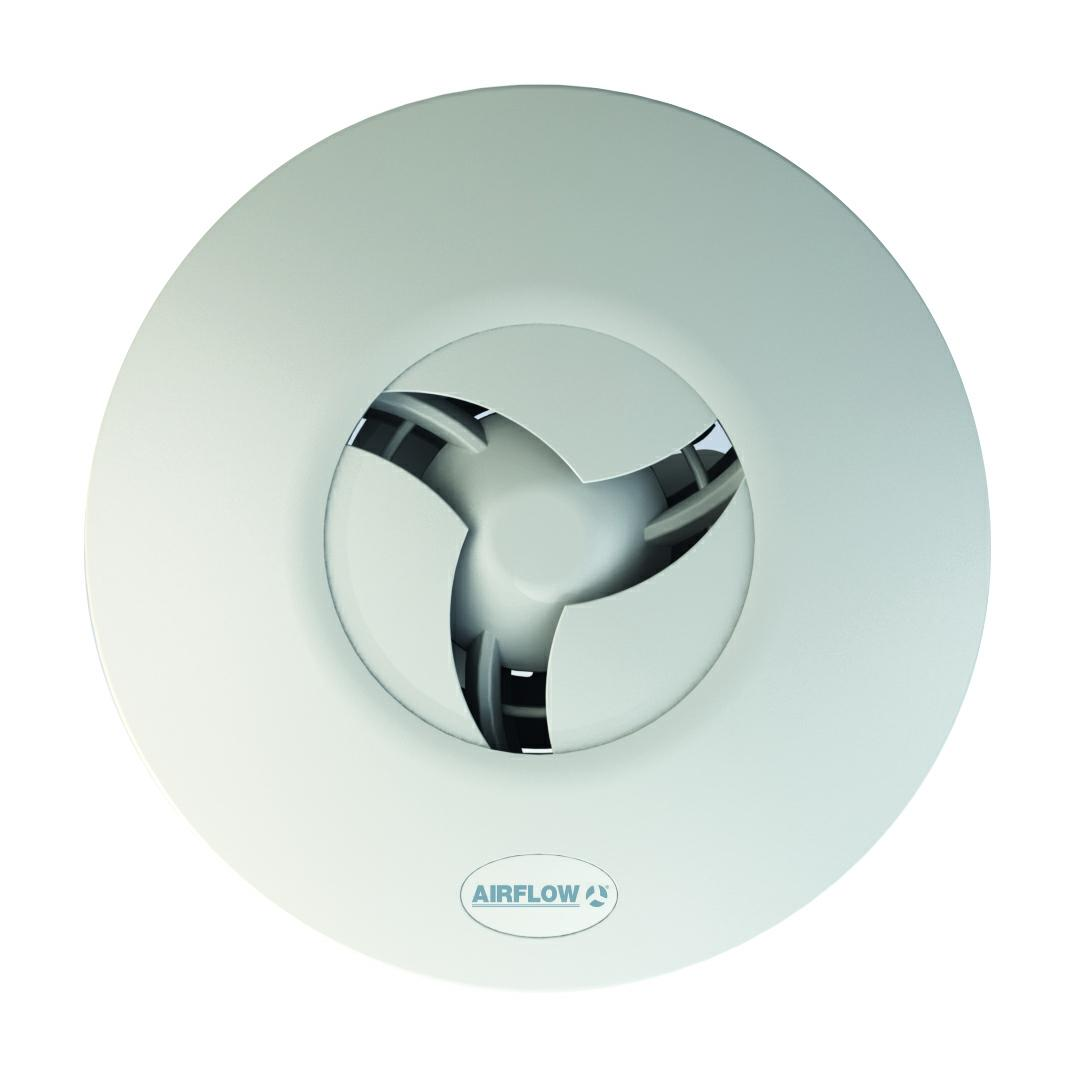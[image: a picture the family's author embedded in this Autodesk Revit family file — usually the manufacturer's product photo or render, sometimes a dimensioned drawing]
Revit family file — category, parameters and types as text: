
# Revit family: CADS_AIRFLOWdev_Fan_iCON15L_Smart
name_source: partatom
category: Mechanical Equipment
revit_build: Autodesk Revit 2016 (Build: 20150220_1215(x64)
units: mm (PartAtom-declared; Revit-internal decimal feet)

## family parameters
Cut with Voids When Loaded = No
Host = Face
Part Type = Normal
Room Calculation Point = No
Round Connector Dimension = Use Diameter
Shared = No

## types (1)
- iCONsmart 15L
    6MonthlyMaintenance = Visually inspect system, clean the fan and ducting if necessary
    A = 194 mm  [stored 0.636483 ft]
    AccessClearanceBottom = 350 mm
    AccessClearanceFront = 350 mm
    AccessClearanceLeft = 350 mm
    AccessClearanceRear = 0 mm  [stored 0 ft]
    AccessClearanceRight = 350 mm
    AccessClearanceTop = 350 mm
    AnthraciteFT = CADS_AIRFLOWdev_Fan_iCON15_Covers : Anthracite
    AssemblyPlace = UKNOWN
    AssetType = Fixed
    BMSLinks = No
    Body = CADS_AirFlow_White
    C = 72 mm  [stored 0.23622 ft]
    CADS_Index = 0
    CEApproval = Yes
    CapacityControlType = Variable Speed Drive
    Category = Pr_65_67_29_05:Axial Flow Fans
    ChromeFT = CADS_AIRFLOWdev_Fan_iCON15_Covers : Chrome
    Color = White
    Controls = Basic on/off functionality controlled by external switch
The following additional, interchangeable modules can be fitted to the iCONsmart15:
Timer (72687224)
Humidity with Timer (72687225)
Motion sensor with timer  (72687226)
Motion sensor humidity timer (72687227)
    D = 100 mm  [stored 0.328084 ft]
    Default Elevation = 1219 mm
    Description = A smart intermittent extract fan with interchangeable modular controls and covers and a Red Dot Design Award winner and Quiet mark certified
    DesignOfDomesticVentilation = This fan should provide the minimum flow rates outlined and installed in line with Approved Document Part F of the Building Regulations.
    Ductwork = 100mm flexible or rigid
    DurationUnit = Year
    E = 46 mm  [stored 0.150919 ft]
    ErPEnergyRating = C
    ErPFiche = https://www.airflow.com
    Exclusions = Hasn't been installed or used in accordance with the instructions
Connected with an unsuitable electrical supply
Has been misused, neglected or damaged
Modified or repaired by someone not authorised by Airflow Developments Ltd
Hasn't been installed according to Building Regulations or IEEE wiring regulations
    ExpectedServiceLife = 5
    ExternalExhaustAirTerminals = 90% free air grille
    Fan = Domestic intermittent axial fan
    Features = Smart intermittent
    Finish = Matte
    FireControlPanelLinks = No
    GlobalTradeItemNumber = 5019009325873
    Grade = Virgin
    GrossWeight = 0.70 kg
    HT = iCON_Smart_Modules : Humidity Timer
    HasPartWinding = Yes
    HasProtectiveEarth = No
    IP_Code = IPX5
    ISO140001 = Yes
    ISO90001 = Yes
    IfcExportAs = IfcFanType
    IfcExportType = NOTDEFINED
    InsulationStandardClass = Double Insulated
    IsExtendedWarranty = No
    IsGuarded = Yes
    MSHT = iCON_Smart_Modules : Motion Sensor Humidity Timer
    MST = iCON_Smart_Modules : Motion Sensor Timer
    Manufacturer = Airflow Developments Ltd
    ManufacturerAddress = Aidelle House
Lancaster Road
Cressex Business Park
High Wycombe
Bucks
HP123QP
    ManufacturerTelephone = 01494 525252
    ManufacturerWebsite = www.airflow.com
    Material = Plastic
    ModelLabel = iCONsmart 15L
    ModelReference = 72687221
    MotorDriveType = Direct Drive
    MotorEnclosureType = Totally Enclosed Air Over
    NBSCode = 90-45-30/310 Axial flow fans;
    NominalAirFlowRate = 22.0 L/s
    NominalFrequencyRange = 50-60
    NominalHeight = 194 mm  [stored 0.636483 ft]
    NominalLength = 118 mm
    NominalPowerRate = 3 W
    NominalRotationSpeed = 2500 Hz
    NominalStaticPressure = 98.4 Pa
    NominalWidth = 194 mm  [stored 0.636483 ft]
    NumberOfPoles = 1
    OperationAndMaintenanceManual = https://www.airflow.com
    OperationAndMaintenanceManualAccessories = https://www.airflow.com
    OperationTemperatureRange = up to 40°C
    PointOfContact = Airflow Developments Ltd
    PowerSource = System-powered
    PressureCurve = https://www.airflow.com
    ProductLiterature = https://www.airflow.com
    ProductLiteratureAccessories = https://www.airflow.com
    ProductionYear = 2017
    Quantity = 1
    QuietMarkApproval = Yes
    RatedCurrent = 3 A
    RatedVoltage = 21 V
    RedDotDesignAward = Yes
    ReplacementCost = 166.64
    RoomExtractAirTerminalDevices = En-suite, toilet and bathroom fan
    SandstoneFT = CADS_AIRFLOWdev_Fan_iCON15_Covers : Standstone
    ServiceLifeDuration = 5
    ServiceLifeType = ExpectedServiceLife
    Shape = Round
    ShippingWeight = 0.90 kg
    SilverFT = CADS_AIRFLOWdev_Fan_iCON15_Covers : Silver
    Size = 118 x 194 x 194
    StartingTime = 5.0 s
    Status = New
    SupplyPhase = 1
    TM = iCON_Smart_Modules : Timer
    Type = ICSM15
    Type Image = CADS_AIRFLOWdev_Fan_iCON15L_Smart.jpg
    Uniclass2015 = Pr_65_67_29_05
    WarrantyContent = Covered against faulty material or workmanship - not reinstallation if needed
    WarrantyGuarantor = Airflow Developments Ltd
    WarrantyPeriod = 5
    WarrantyPeriodForMotors = 1
    WarrantyPeriodWhenRegistered = 5

note: [stored X ft] marks values corroborated as IEEE doubles in the binary element streams (Revit-internal decimal feet)

## geometry (parser evidence)
native form markers: Blend x2, Sweep x6
no freeform markers — native parametric forms only
